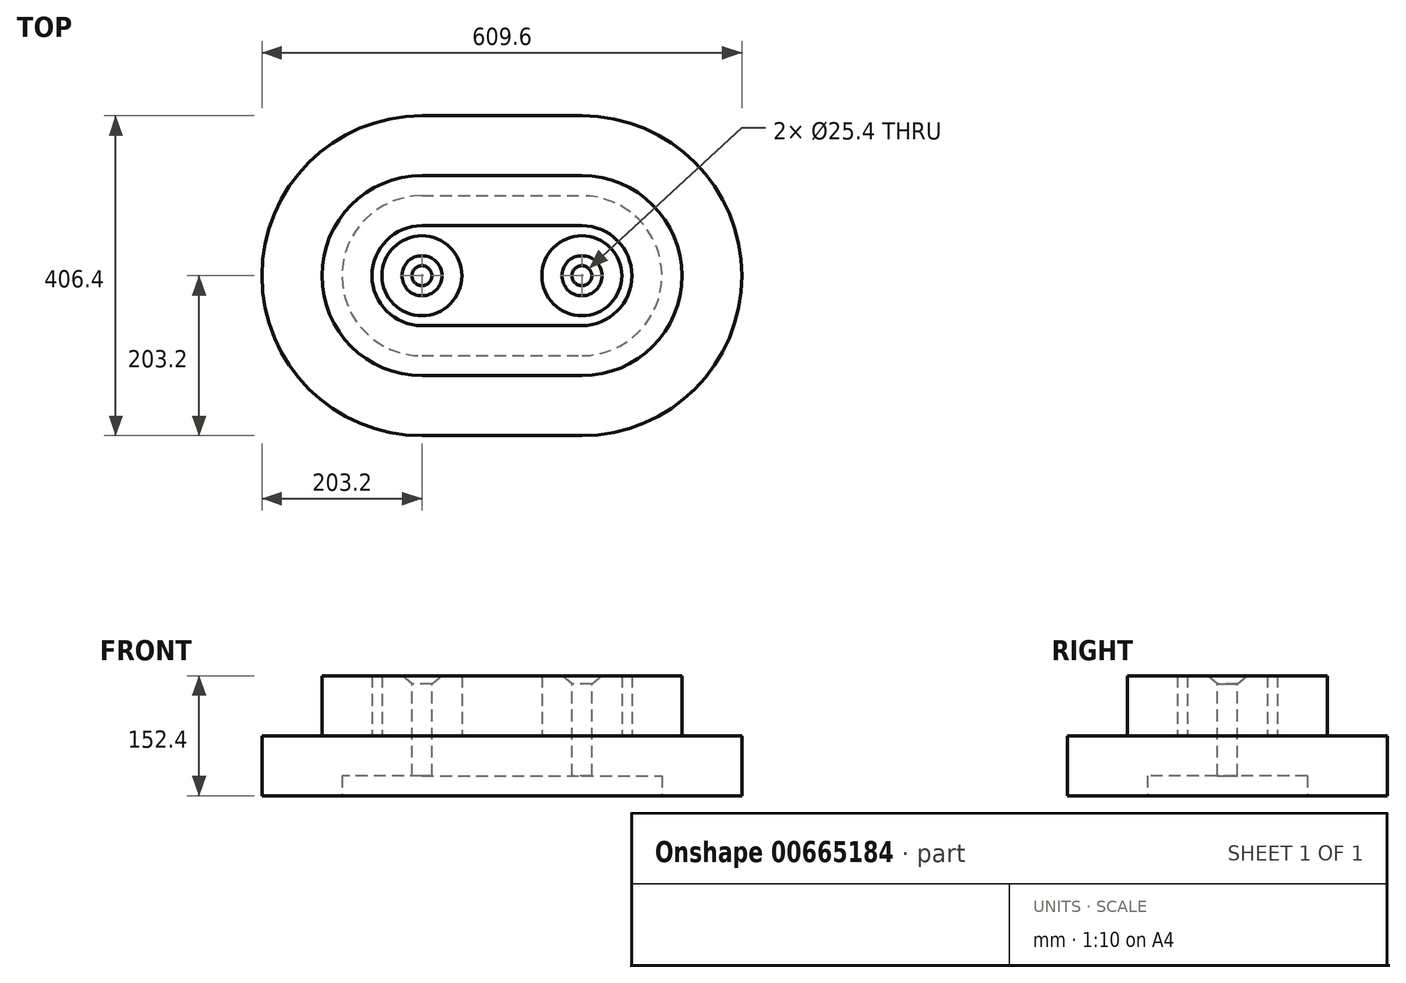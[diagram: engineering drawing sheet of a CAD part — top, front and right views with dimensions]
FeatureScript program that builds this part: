
annotation { "Feature Type Name" : "Feature", "Feature Type Description" : "" }
export const myFeature = defineFeature(function(context is Context, id is Id, definition is map)
    precondition{}
    {
        {
            var Q0;
            Q0=qCreatedBy(makeId("Top.planeOp"),FACE);
            var sketch = newSketch(context, id + "F0", { "sketchPlane" : qUnion([Q0])});
            skCircle(sketch, "E0", {"center": v(101.6, 0) * mm, "radius": 25.4 * mm});
            skCircle(sketch, "E1", {"center": v(101.6, 0) * mm, "radius": 50.8 * mm});
            skArc(sketch, "E2", {"start": v(101.6, -63.5) * mm, "mid": v(165.1, 0) * mm, "end": v(101.6, 63.5) * mm});
            skCircle(sketch, "E3", {"center": v(-101.6, 0) * mm, "radius": 25.4 * mm});
            skCircle(sketch, "E4", {"center": v(-101.6, 0) * mm, "radius": 50.8 * mm});
            skArc(sketch, "E5", {"start": v(-101.6, 63.5) * mm, "mid": v(-165.1, 0) * mm, "end": v(-101.6, -63.5) * mm});
            skLineSegment(sketch, "E6", {"start": v(-101.6, -63.5) * mm, "end": v(101.6, -63.5) * mm});
            skLineSegment(sketch, "E7", {"start": v(-101.6, 63.5) * mm, "end": v(101.6, 63.5) * mm});
            skArc(sketch, "E8", {"start": v(-101.6, 127) * mm, "mid": v(-228.6, 0) * mm, "end": v(-101.6, -127) * mm});
            skArc(sketch, "E9", {"start": v(101.6, -127) * mm, "mid": v(228.6, 0) * mm, "end": v(101.6, 127) * mm});
            skLineSegment(sketch, "E10", {"start": v(-101.6, 127) * mm, "end": v(101.6, 127) * mm});
            skLineSegment(sketch, "E11", {"start": v(-101.6, -127) * mm, "end": v(101.6, -127) * mm});
            skArc(sketch, "E12", {"start": v(-101.6, 203.2) * mm, "mid": v(-304.8, 0) * mm, "end": v(-101.6, -203.2) * mm});
            skLineSegment(sketch, "E13", {"start": v(-101.6, 203.2) * mm, "end": v(101.6, 203.2) * mm});
            skLineSegment(sketch, "E14", {"start": v(-101.6, -203.2) * mm, "end": v(101.6, -203.2) * mm});
            skArc(sketch, "E15.trimOffspring", {"start": v(101.6, -203.2) * mm, "mid": v(304.8, 0) * mm, "end": v(101.6, 203.2) * mm});
            skLineSegment(sketch, "E16", {"start": v(-101.6, 0) * mm, "end": v(101.6, 0) * mm, "construction": true});
            skSolve(sketch);
        }
        {
            var Q0;
            Q0=makeQuery(id+"F0.imprint","IMPRINT",FACE,{"disambiguationData":[TD([[makeQuery(id+"F0.imprint","IMPRINT",EDGE,{"derivedFrom":sQuery(id+"F0.wireOp",EDGE,"E8")}),-1.0]])]});
            var Q1;
            Q1=makeQuery(id+"F0.imprint","IMPRINT",FACE,{"disambiguationData":[TD([[makeQuery(id+"F0.imprint","IMPRINT",EDGE,{"derivedFrom":sQuery(id+"F0.wireOp",EDGE,"E2")}),-1.0]])]});
            var Q2;
            Q2=makeQuery(id+"F0.imprint","IMPRINT",FACE,{"disambiguationData":[TD([[makeQuery(id+"F0.imprint","IMPRINT",EDGE,{"derivedFrom":sQuery(id+"F0.wireOp",EDGE,"E1")}),-1.0]])]});
            var Q3;
            Q3=makeQuery(id+"F0.imprint","IMPRINT",FACE,{"disambiguationData":[TD([[makeQuery(id+"F0.imprint","IMPRINT",EDGE,{"derivedFrom":sQuery(id+"F0.wireOp",EDGE,"E3")}),-1.0]])]});
            var Q4;
            Q4=makeQuery(id+"F0.imprint","IMPRINT",FACE,{"disambiguationData":[TD([[makeQuery(id+"F0.imprint","IMPRINT",EDGE,{"derivedFrom":sQuery(id+"F0.wireOp",EDGE,"RiiItPTW-P9aj-dTSl-eAIZ-IVZ0qJKBElgp")}),-1.0]])]});
            var Q5;
            Q5=makeQuery(id+"F0.imprint","IMPRINT",FACE,{"disambiguationData":[TD([[makeQuery(id+"F0.imprint","IMPRINT",EDGE,{"derivedFrom":sQuery(id+"F0.wireOp",EDGE,"E0")}),-1.0]])]});
            var Q6;
            Q6=makeQuery(id+"F0.imprint","IMPRINT",FACE,{"disambiguationData":[TD([[makeQuery(id+"F0.imprint","IMPRINT",EDGE,{"derivedFrom":sQuery(id+"F0.wireOp",EDGE,"P1xPbjmz-qN18-2DK3-KT4p-KpfQuWqCBaTF")}),-1.0]])]});
            var Q7;
            Q7=makeQuery(id+"F0.imprint","IMPRINT",FACE,{"disambiguationData":[TD([[makeQuery(id+"F0.imprint","IMPRINT",EDGE,{"derivedFrom":sQuery(id+"F0.wireOp",EDGE,"E3")}),1.0]])]});
            var Q8;
            Q8=makeQuery(id+"F0.imprint","IMPRINT",FACE,{"disambiguationData":[TD([[makeQuery(id+"F0.imprint","IMPRINT",EDGE,{"derivedFrom":sQuery(id+"F0.wireOp",EDGE,"E0")}),1.0]])]});
            extrude(context, id + "F1", {"entities" : qUnion([Q0, Q1, Q2, Q3, Q4, Q5, Q6, Q7, Q8]), "depth" : 76.2 * mm, "offsetDistance" : 25.4 * mm});
        }
        {
            var Q0;
            Q0=makeQuery(id+"F0.imprint","IMPRINT",FACE,{"disambiguationData":[TD([[makeQuery(id+"F0.imprint","IMPRINT",EDGE,{"derivedFrom":sQuery(id+"F0.wireOp",EDGE,"E2")}),-1.0]])]});
            var Q1;
            Q1=makeQuery(id+"F0.imprint","IMPRINT",FACE,{"disambiguationData":[TD([[makeQuery(id+"F0.imprint","IMPRINT",EDGE,{"derivedFrom":sQuery(id+"F0.wireOp",EDGE,"E0")}),-1.0]])]});
            var Q2;
            Q2=makeQuery(id+"F0.imprint","IMPRINT",FACE,{"disambiguationData":[TD([[makeQuery(id+"F0.imprint","IMPRINT",EDGE,{"derivedFrom":sQuery(id+"F0.wireOp",EDGE,"E3")}),-1.0]])]});
            var Q3;
            Q3=makeQuery(id+"F0.imprint","IMPRINT",FACE,{"disambiguationData":[TD([[makeQuery(id+"F0.imprint","IMPRINT",EDGE,{"derivedFrom":sQuery(id+"F0.wireOp",EDGE,"E0")}),1.0]])]});
            var Q4;
            Q4=makeQuery(id+"F0.imprint","IMPRINT",FACE,{"disambiguationData":[TD([[makeQuery(id+"F0.imprint","IMPRINT",EDGE,{"derivedFrom":sQuery(id+"F0.wireOp",EDGE,"E3")}),1.0]])]});
            extrude(context, id + "F2", {"entities" : qUnion([Q0, Q1, Q2, Q3, Q4]), "operationType" : NewBodyOperationType.ADD, "depth" : 152.4 * mm, "offsetDistance" : 25.4 * mm});
        }
        {
            var Q0;
            Q0=makeQuery(id+"F0.imprint","IMPRINT",FACE,{"disambiguationData":[TD([[makeQuery(id+"F0.imprint","IMPRINT",EDGE,{"derivedFrom":sQuery(id+"F0.wireOp",EDGE,"E2")}),-1.0]])]});
            var sketch = newSketch(context, id + "F3", { "sketchPlane" : qUnion([Q0])});
            skArc(sketch, "E17", {"start": v(-101.6, 101.6) * mm, "mid": v(-203.2, 0) * mm, "end": v(-101.6, -101.6) * mm});
            skArc(sketch, "E18", {"start": v(101.6, -101.6) * mm, "mid": v(203.2, 0) * mm, "end": v(101.6, 101.6) * mm});
            skLineSegment(sketch, "E19", {"start": v(-101.6, -101.6) * mm, "end": v(101.6, -101.6) * mm});
            skLineSegment(sketch, "E20", {"start": v(-101.6, 101.6) * mm, "end": v(101.6, 101.6) * mm});
            skSolve(sketch);
        }
        {
            var Q0;
            Q0 = qSketchRegion(id + "F3", true);
            extrude(context, id + "F4", {"entities" : qUnion([Q0]), "operationType" : NewBodyOperationType.REMOVE, "depth" : 25.4 * mm, "offsetDistance" : 25.4 * mm});
        }
        {
            var Q0;
            Q0=makeQuery(id+"F2.opExtrude","CAP_FACE",FACE,{"disambiguationData":[OSD([sQuery(id+"F0.wireOp",EDGE,"E1")])],"isStart":false});
            var sketch = newSketch(context, id + "F5", { "sketchPlane" : qUnion([Q0])});
            skPoint(sketch, "E21.0", {"position": v(101.6, 0) * mm});
            skPoint(sketch, "E22.0", {"position": v(-101.6, 0) * mm});
            skSolve(sketch);
        }
        {
            var Q0;
            Q0=sQuery(id+"F5.wireOp",VERTEX,"E22.0");
            var Q1;
            Q1=sQuery(id+"F5.wireOp",VERTEX,"E21.0");
            var Q2;
            Q2=makeQuery(id+"F1.opExtrude","SWEPT_BODY",BODY,{"disambiguationData":[OSD([sQuery(id+"F0.wireOp",EDGE,"E12"),sQuery(id+"F0.wireOp",EDGE,"E13"),sQuery(id+"F0.wireOp",EDGE,"E14"),sQuery(id+"F0.wireOp",EDGE,"E15.trimOffspring")])]});
            hole(context, id + "F6", {"style" : HoleStyle.C_SINK, "endStyle" : HoleEndStyle.THROUGH, "holeDiameter" : 25.4 * mm, "cSinkDiameter" : 50.8 * mm, "cSinkAngle" : 100 * degree, "majorDiameter" : 6.35 * mm, "isTappedThrough" : true, "tappedDepth" : 12.7 * mm, "tapClearance" : 3, "locations" : qUnion([Q0, Q1]), "scope" : qUnion([Q2])});
        }
    });
